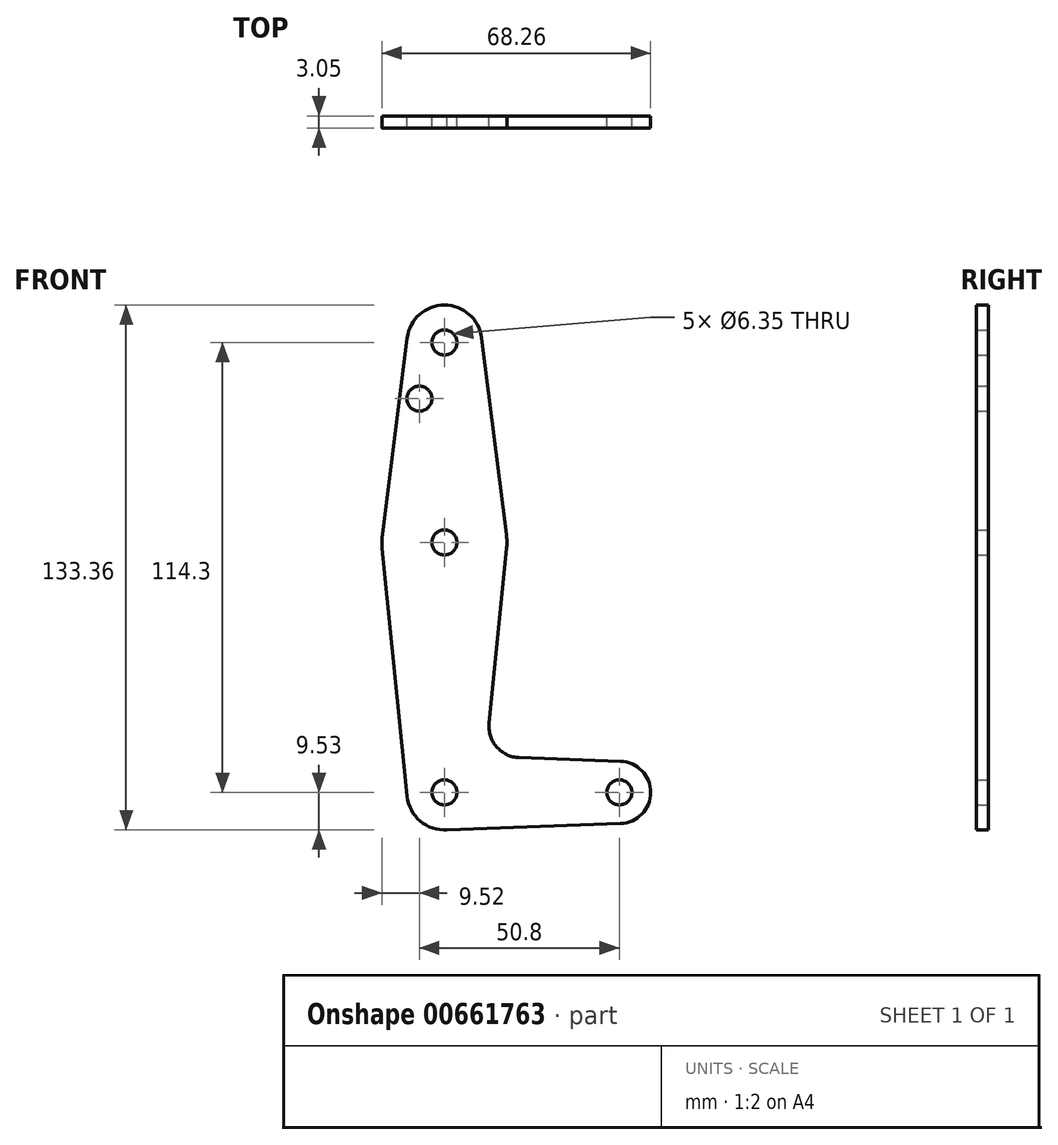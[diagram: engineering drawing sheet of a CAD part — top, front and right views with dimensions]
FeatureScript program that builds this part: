
annotation { "Feature Type Name" : "Feature", "Feature Type Description" : "" }
export const myFeature = defineFeature(function(context is Context, id is Id, definition is map)
    precondition{}
    {
        {
            var Q0;
            Q0=qCreatedBy(makeId("Front.planeOp"),FACE);
            var sketch = newSketch(context, id + "F0", { "sketchPlane" : qUnion([Q0])});
            skCircle(sketch, "E0", {"center": v(0, 0) * mm, "radius": 9.53 * mm});
            skCircle(sketch, "E1", {"center": v(0, 63.5) * mm, "radius": 15.88 * mm});
            skCircle(sketch, "E2", {"center": v(0, 114.3) * mm, "radius": 9.53 * mm});
            skCircle(sketch, "E3", {"center": v(44.45, 0) * mm, "radius": 7.94 * mm});
            skLineSegment(sketch, "E4", {"start": v(-9.45, 115.5) * mm, "end": v(-15.75, 65.48) * mm});
            skLineSegment(sketch, "E5", {"start": v(9.45, 115.5) * mm, "end": v(15.75, 65.48) * mm});
            skLineSegment(sketch, "E6", {"start": v(-15.8, 61.91) * mm, "end": v(-9.48, -0.95) * mm});
            skLineSegment(sketch, "E7", {"start": v(15.8, 61.91) * mm, "end": v(11.34, 17.59) * mm});
            skLineSegment(sketch, "E8", {"start": v(18.97, 8.85) * mm, "end": v(44.73, 7.93) * mm});
            skLineSegment(sketch, "E9", {"start": v(0, -9.53) * mm, "end": v(44.73, -7.93) * mm});
            skCircle(sketch, "E10", {"center": v(0, 114.3) * mm, "radius": 3.18 * mm});
            skCircle(sketch, "E11", {"center": v(0, 63.5) * mm, "radius": 3.18 * mm});
            skCircle(sketch, "E12", {"center": v(0, 0) * mm, "radius": 3.18 * mm});
            skCircle(sketch, "E13", {"center": v(44.45, 0) * mm, "radius": 3.18 * mm});
            skPoint(sketch, "E14.newPointA", {"position": v(0, 9.53) * mm});
            skArc(sketch, "E14.filletArc", {"start": v(11.34, 17.59) * mm, "mid": v(13.26, 11.57) * mm, "end": v(18.97, 8.85) * mm});
            skCircle(sketch, "E15.MirrorC", {"center": v(-6.35, 100.03) * mm, "radius": 3.18 * mm});
            skLineSegment(sketch, "E16", {"start": v(0, 114.3) * mm, "end": v(0, 0) * mm, "construction": true});
            skSolve(sketch);
        }
        {
            var Q0;
            Q0=qSketchRegion(id+"F0",true);
            extrude(context, id + "F1", {"entities" : qUnion([Q0]), "depth" : 3.05 * mm});
        }
    });
